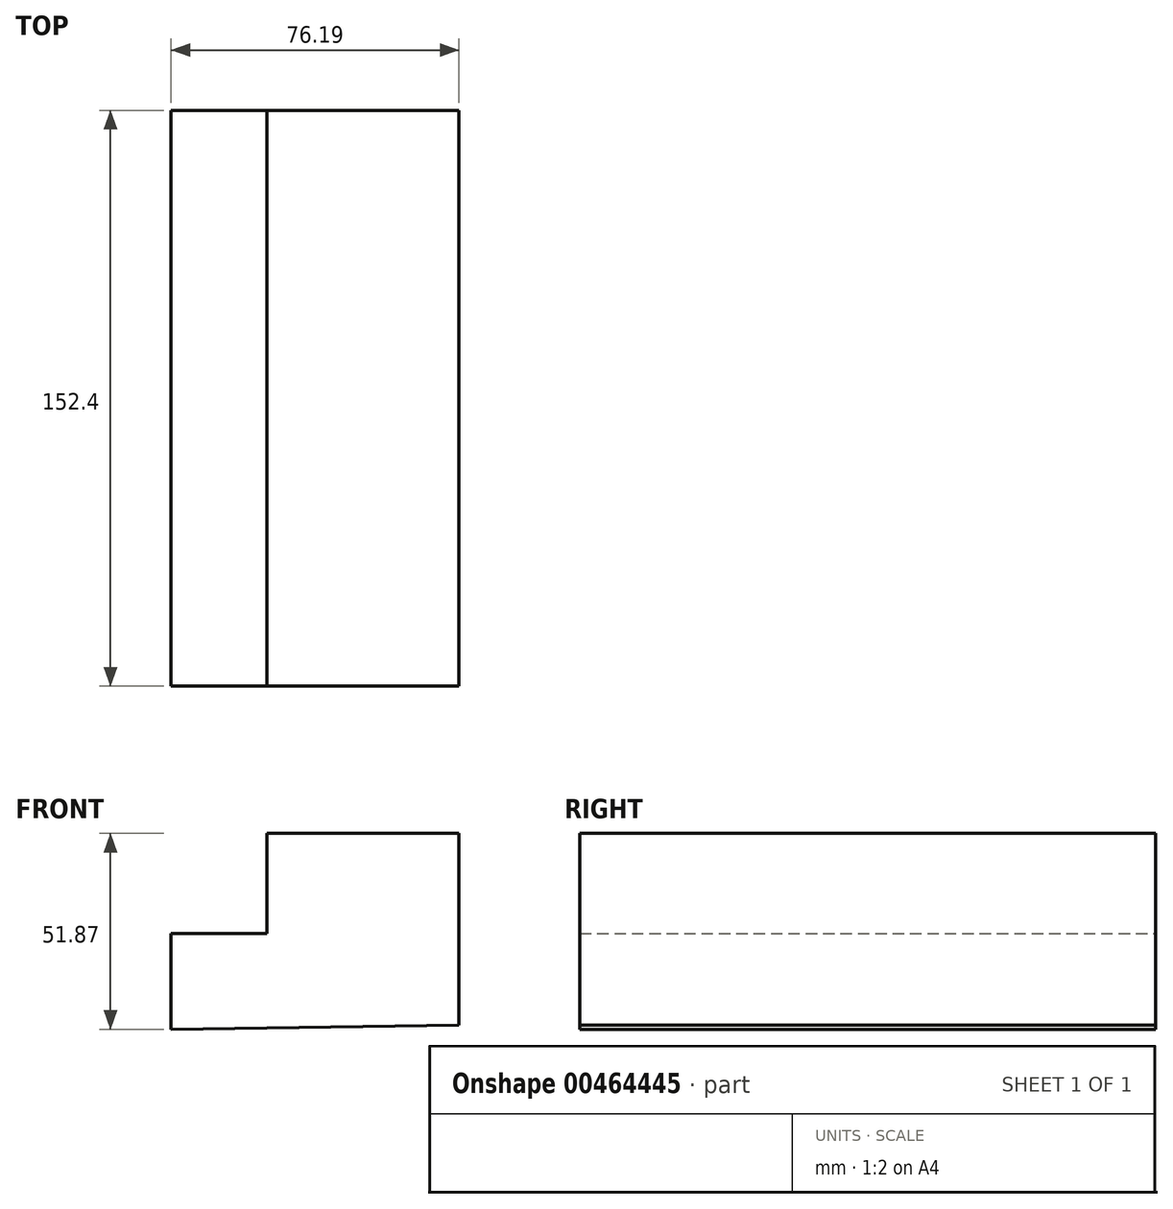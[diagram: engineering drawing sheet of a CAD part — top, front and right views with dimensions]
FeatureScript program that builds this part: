
annotation { "Feature Type Name" : "Feature", "Feature Type Description" : "" }
export const myFeature = defineFeature(function(context is Context, id is Id, definition is map)
    precondition{}
    {
        {
            var Q0;
            Q0=qCreatedBy(makeId("Front.planeOp"),FACE);
            var sketch = newSketch(context, id + "F0", { "sketchPlane" : qUnion([Q0])});
            skLineSegment(sketch, "E0", {"start": v(76.2, 88.42) * mm, "end": v(25.4, 88.42) * mm});
            skLineSegment(sketch, "E1", {"start": v(25.4, 88.42) * mm, "end": v(25.4, 61.95) * mm});
            skLineSegment(sketch, "E2", {"start": v(25.4, 61.95) * mm, "end": v(0, 61.95) * mm});
            skLineSegment(sketch, "E3", {"start": v(0, 61.95) * mm, "end": v(0, 36.55) * mm});
            skLineSegment(sketch, "E4", {"start": v(0, 36.55) * mm, "end": v(76.2, 37.62) * mm});
            skLineSegment(sketch, "E5", {"start": v(76.2, 37.62) * mm, "end": v(76.2, 88.42) * mm});
            skSolve(sketch);
        }
        {
            var Q0;
            Q0 = qSketchRegion(id + "F0", true);
            extrude(context, id + "F1", {"entities" : qUnion([Q0]), "depth" : 152.4 * mm});
        }
    });
